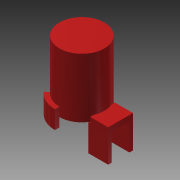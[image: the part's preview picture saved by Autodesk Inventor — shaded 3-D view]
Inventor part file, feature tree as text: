
AUTODESK INVENTOR PART (.ipt)
format: ipt  version: 2013 (Build 170138000, 138)  size: 165,376 bytes
history: native  units: mm
features: extrude x6, sketch x6, other x1
ambient origin geometry x8: Origin, YZ Plane, XZ Plane, XY Plane, X Axis, Y Axis, Z Axis, Center Point
feature tree (13):
  other  "ソリッド1"
  extrude  "押し出し1"  Depth=9.768mm
  extrude  "押し出し2"  Depth=15.0mm
  extrude  "押し出し3"  Depth=2.0mm
  extrude  "押し出し4"  Depth=18.0mm
  extrude  "押し出し5"  Depth=13.768mm
  extrude  "押し出し6"  Depth=10.0mm TaperAngle=0.0deg
  sketch  "スケッチ1"
  sketch  "スケッチ2"
  sketch  "スケッチ3"
  sketch  "スケッチ4"
  sketch  "スケッチ6"
  sketch  "スケッチ7"
